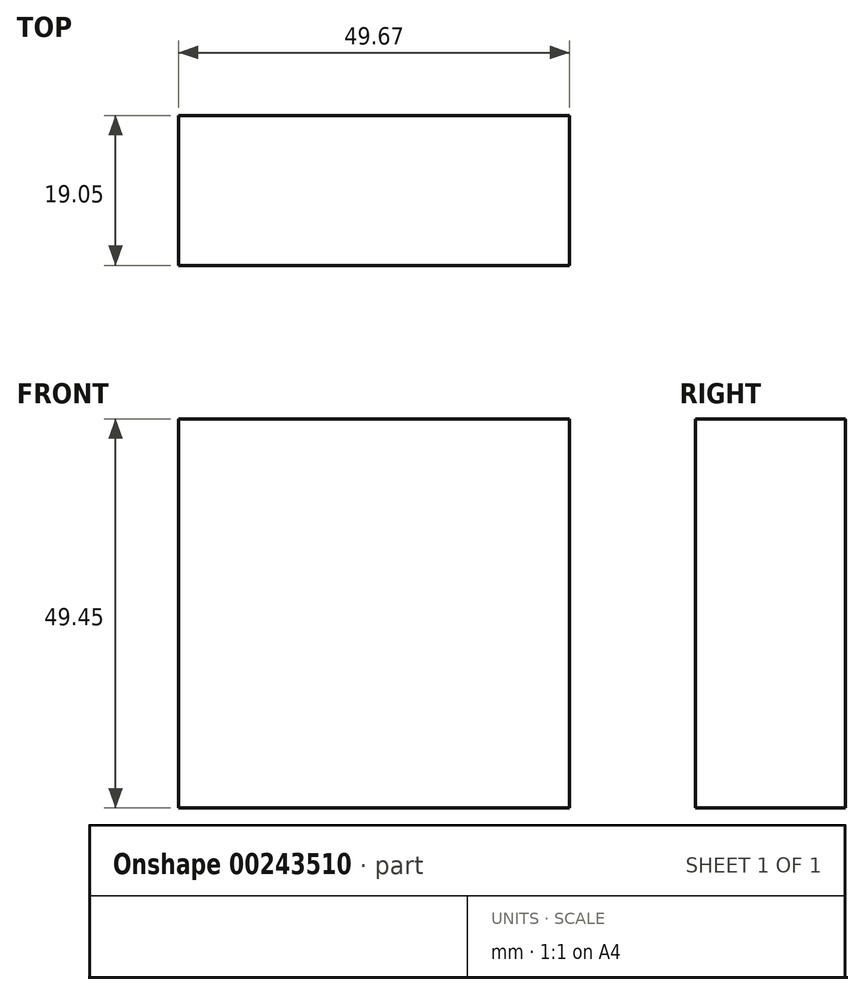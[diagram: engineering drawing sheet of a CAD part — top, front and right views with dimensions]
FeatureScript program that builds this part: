
annotation { "Feature Type Name" : "Feature", "Feature Type Description" : "" }
export const myFeature = defineFeature(function(context is Context, id is Id, definition is map)
    precondition{}
    {
        {
            var Q0;
            Q0=qCreatedBy(makeId("Front.planeOp"),FACE);
            var sketch = newSketch(context, id + "F0", { "sketchPlane" : qUnion([Q0])});
            skLineSegment(sketch, "E0.bottom", {"start": v(0, 0) * mm, "end": v(-49.67, 0) * mm});
            skLineSegment(sketch, "E0.top", {"start": v(0, 49.45) * mm, "end": v(-49.67, 49.45) * mm});
            skLineSegment(sketch, "E0.left", {"start": v(0, 0) * mm, "end": v(0, 49.45) * mm});
            skLineSegment(sketch, "E0.right", {"start": v(-49.67, 0) * mm, "end": v(-49.67, 49.45) * mm});
            skSolve(sketch);
        }
        {
            var Q0;
            Q0=makeQuery(id+"F0.imprint","IMPRINT",FACE,{"disambiguationData":[TD([[makeQuery(id+"F0.imprint","IMPRINT",EDGE,{"derivedFrom":sQuery(id+"F0.wireOp",EDGE,"E0.bottom")}),-1.0]])]});
            extrude(context, id + "F1", {"entities" : qUnion([Q0]), "depth" : 19.05 * mm});
        }
    });
